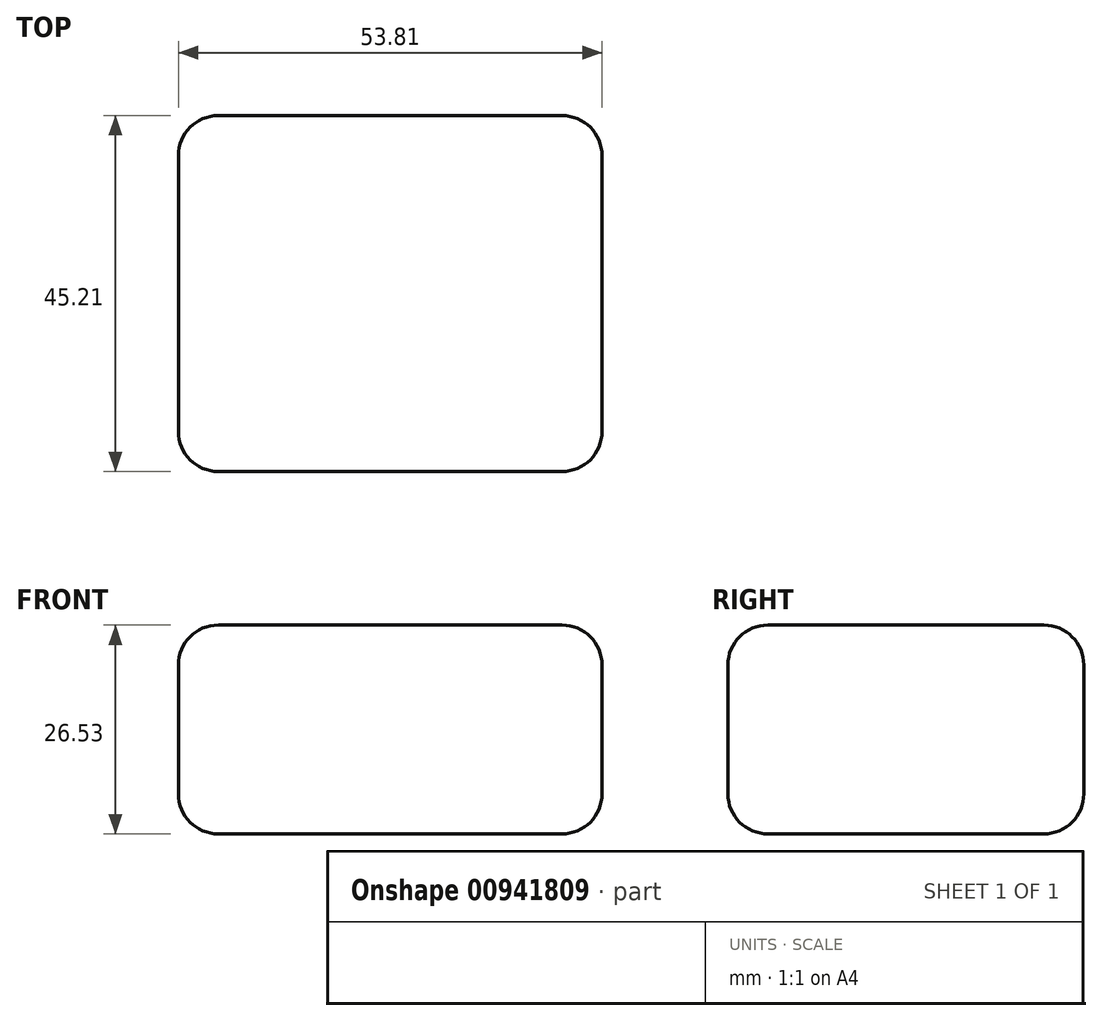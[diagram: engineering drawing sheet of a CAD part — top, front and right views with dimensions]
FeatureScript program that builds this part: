
annotation { "Feature Type Name" : "Feature", "Feature Type Description" : "" }
export const myFeature = defineFeature(function(context is Context, id is Id, definition is map)
    precondition{}
    {
        {
            var Q0;
            Q0=qCreatedBy(makeId("Front.planeOp"),FACE);
            var sketch = newSketch(context, id + "F0", { "sketchPlane" : qUnion([Q0])});
            skLineSegment(sketch, "E0", {"start": v(-53.8, 32.9) * mm, "end": v(-53.8, 6.37) * mm});
            skLineSegment(sketch, "E1", {"start": v(-53.8, 6.37) * mm, "end": v(0, 6.37) * mm});
            skLineSegment(sketch, "E2", {"start": v(-53.8, 32.9) * mm, "end": v(0, 32.9) * mm});
            skLineSegment(sketch, "E3", {"start": v(0, 32.9) * mm, "end": v(0, 6.37) * mm});
            skSolve(sketch);
        }
        {
            var Q0;
            Q0 = qSketchRegion(id + "F0", true);
            extrude(context, id + "F1", {"entities" : qUnion([Q0]), "depth" : 45.2 * mm, "offsetDistance" : 25.4 * mm});
        }
        {
            var Q0;
            Q0=makeQuery(id+"F1.opExtrude","SWEPT_FACE",FACE,{"disambiguationData":[OSD([sQuery(id+"F0.wireOp",EDGE,"E3")])]});
            var Q1;
            Q1=makeQuery(id+"F1.opExtrude","CAP_FACE",FACE,{"disambiguationData":[OSD([sQuery(id+"F0.wireOp",EDGE,"E0"),sQuery(id+"F0.wireOp",EDGE,"E1"),sQuery(id+"F0.wireOp",EDGE,"E2"),sQuery(id+"F0.wireOp",EDGE,"E3")])],"isStart":false});
            var Q2;
            Q2=makeQuery(id+"F1.opExtrude","SWEPT_FACE",FACE,{"disambiguationData":[OSD([sQuery(id+"F0.wireOp",EDGE,"E2")])]});
            var Q3;
            Q3=makeQuery(id+"F1.opExtrude","SWEPT_FACE",FACE,{"disambiguationData":[OSD([sQuery(id+"F0.wireOp",EDGE,"E0")])]});
            var Q4;
            Q4=makeQuery(id+"F1.opExtrude","CAP_FACE",FACE,{"disambiguationData":[OSD([sQuery(id+"F0.wireOp",EDGE,"E0"),sQuery(id+"F0.wireOp",EDGE,"E1"),sQuery(id+"F0.wireOp",EDGE,"E2"),sQuery(id+"F0.wireOp",EDGE,"E3")])],"isStart":true});
            var Q5;
            Q5=makeQuery(id+"F1.opExtrude","SWEPT_FACE",FACE,{"disambiguationData":[OSD([sQuery(id+"F0.wireOp",EDGE,"E1")])]});
            fillet(context, id + "F2", {"entities" : qUnion([Q0, Q1, Q2, Q3, Q4, Q5]), "radius" : 5.08 * mm, "tangentPropagation" : true, "allowEdgeOverflow" : false});
        }
    });
